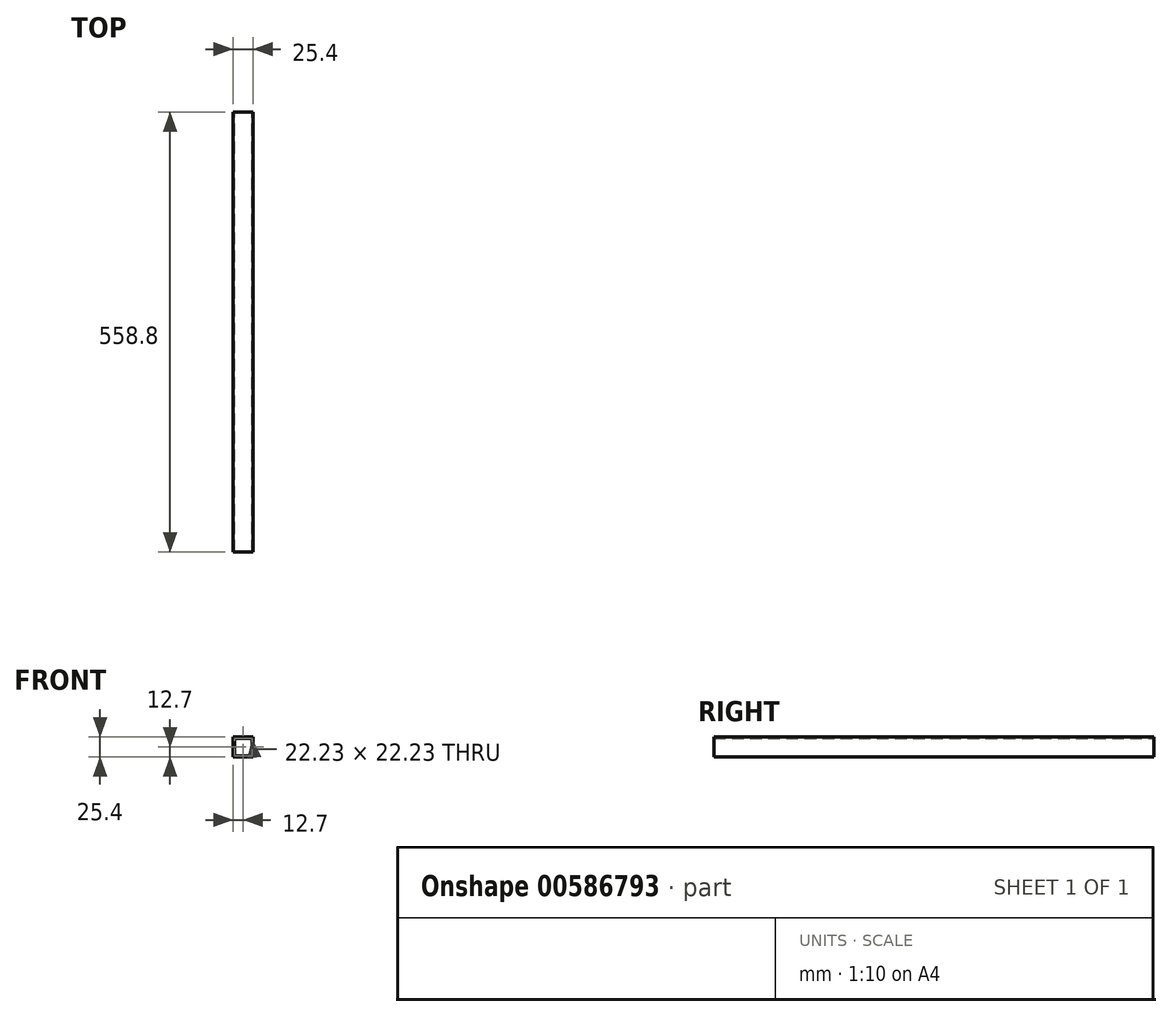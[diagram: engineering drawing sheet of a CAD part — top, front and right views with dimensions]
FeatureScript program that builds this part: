
annotation { "Feature Type Name" : "Feature", "Feature Type Description" : "" }
export const myFeature = defineFeature(function(context is Context, id is Id, definition is map)
    precondition{}
    {
        {
            var Q0;
            Q0=qCreatedBy(makeId("Front.planeOp"),FACE);
            var sketch = newSketch(context, id + "F0", { "sketchPlane" : qUnion([Q0])});
            skLineSegment(sketch, "E0.bottom", {"start": v(12.7, 12.7) * mm, "end": v(-12.7, 12.7) * mm});
            skLineSegment(sketch, "E0.top", {"start": v(12.7, -12.7) * mm, "end": v(-12.7, -12.7) * mm});
            skLineSegment(sketch, "E0.left", {"start": v(12.7, 12.7) * mm, "end": v(12.7, -12.7) * mm});
            skLineSegment(sketch, "E0.right", {"start": v(-12.7, 12.7) * mm, "end": v(-12.7, -12.7) * mm});
            skPoint(sketch, "E0.middle", {"position": v(0, 0) * mm});
            skLineSegment(sketch, "E1.bottom", {"start": v(11.11, 11.11) * mm, "end": v(-11.11, 11.11) * mm});
            skLineSegment(sketch, "E1.top", {"start": v(11.11, -11.11) * mm, "end": v(-11.11, -11.11) * mm});
            skLineSegment(sketch, "E1.left", {"start": v(11.11, 11.11) * mm, "end": v(11.11, -11.11) * mm});
            skLineSegment(sketch, "E1.right", {"start": v(-11.11, 11.11) * mm, "end": v(-11.11, -11.11) * mm});
            skSolve(sketch);
        }
        {
            var Q0;
            Q0=makeQuery(id+"F0.imprint","IMPRINT",FACE,{"disambiguationData":[TD([[makeQuery(id+"F0.imprint","IMPRINT",EDGE,{"derivedFrom":sQuery(id+"F0.wireOp",EDGE,"E0.bottom")}),1.0]])]});
            extrude(context, id + "F1", {"entities" : qUnion([Q0]), "depth" : 558.8 * mm, "offsetDistance" : 25.4 * mm});
        }
    });
